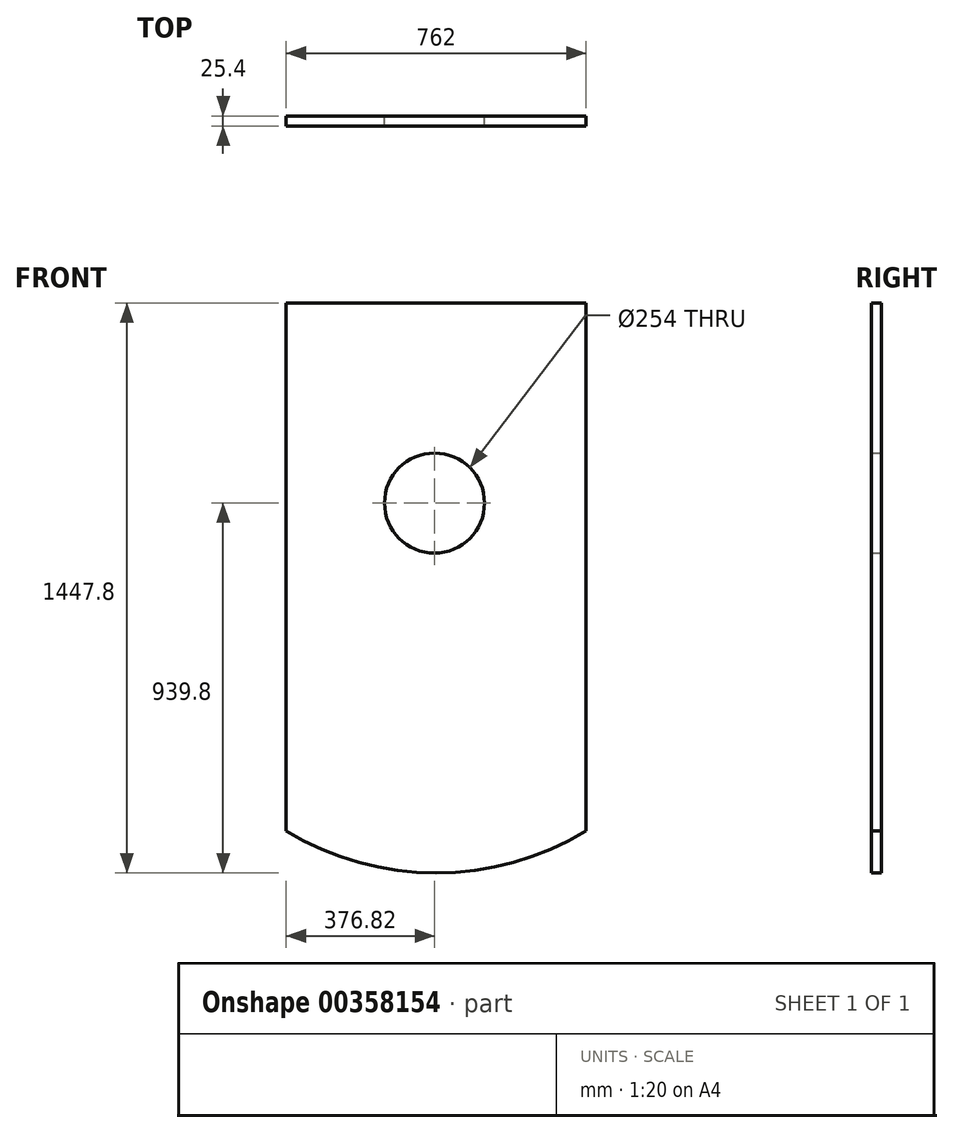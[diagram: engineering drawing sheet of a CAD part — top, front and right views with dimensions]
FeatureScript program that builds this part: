
annotation { "Feature Type Name" : "Feature", "Feature Type Description" : "" }
export const myFeature = defineFeature(function(context is Context, id is Id, definition is map)
    precondition{}
    {
        {
            var Q0;
            Q0=qCreatedBy(makeId("Front.planeOp"),FACE);
            var sketch = newSketch(context, id + "F0", { "sketchPlane" : qUnion([Q0])});
            skCircle(sketch, "E0", {"center": v(0, 0) * mm, "radius": 127 * mm});
            skPoint(sketch, "E1.endSnap0", {"position": v(194.68, 0) * mm});
            skLineSegment(sketch, "E2", {"start": v(385.18, 0) * mm, "end": v(385.18, 508) * mm});
            skLineSegment(sketch, "E3", {"start": v(385.18, 508) * mm, "end": v(-376.82, 508) * mm});
            skLineSegment(sketch, "E4", {"start": v(-376.82, 508) * mm, "end": v(-376.82, -833.61) * mm});
            skLineSegment(sketch, "E5", {"start": v(385.18, 0) * mm, "end": v(385.18, -833.61) * mm});
            skLineSegment(sketch, "E6", {"start": v(-376.82, -939.8) * mm, "end": v(-376.82, -939.8) * mm});
            skLineSegment(sketch, "E7", {"start": v(4.18, 0) * mm, "end": v(4.18, -126.93) * mm});
            skArc(sketch, "E8", {"start": v(-376.82, -833.61) * mm, "mid": v(4.18, -939.8) * mm, "end": v(385.18, -833.61) * mm});
            skSolve(sketch);
        }
        {
            var Q0;
            Q0=makeQuery(id+"F0.imprint","IMPRINT",FACE,{"disambiguationData":[TD([[makeQuery(id+"F0.imprint","IMPRINT",EDGE,{"derivedFrom":sQuery(id+"F0.wireOp",EDGE,"E0")}),-1.0]])]});
            extrude(context, id + "F1", {"entities" : qUnion([Q0]), "depth" : 25.4 * mm});
        }
    });
